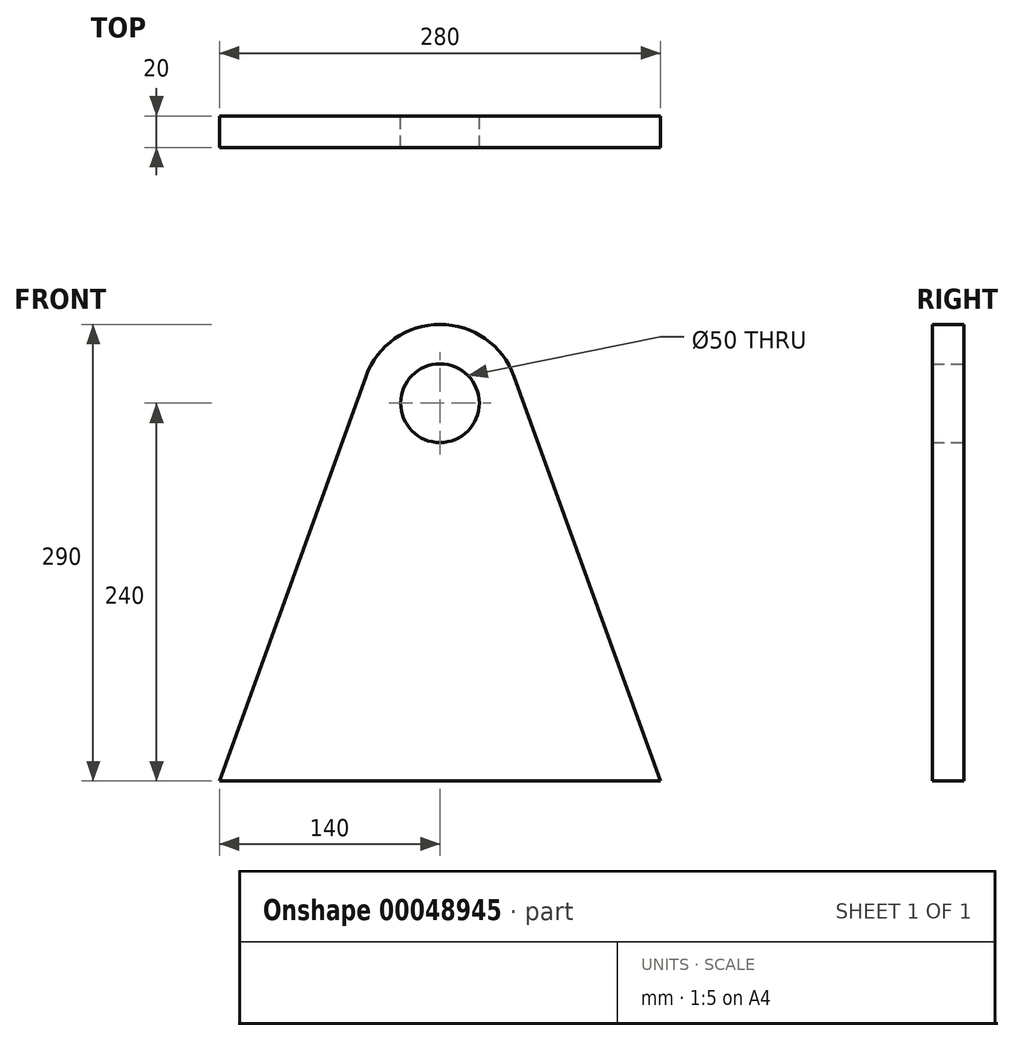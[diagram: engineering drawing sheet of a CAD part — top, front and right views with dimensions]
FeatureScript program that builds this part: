
annotation { "Feature Type Name" : "Feature", "Feature Type Description" : "" }
export const myFeature = defineFeature(function(context is Context, id is Id, definition is map)
    precondition{}
    {
        {
            var Q0;
            Q0=qCreatedBy(makeId("Front.planeOp"),FACE);
            var sketch = newSketch(context, id + "F0", { "sketchPlane" : qUnion([Q0])});
            skLineSegment(sketch, "E0", {"start": v(0, 240) * mm, "end": v(0, 0) * mm, "construction": true});
            skLineSegment(sketch, "E1", {"start": v(0, 0) * mm, "end": v(-140, 0) * mm});
            skLineSegment(sketch, "E2", {"start": v(-53.17, 240) * mm, "end": v(0, 240) * mm, "construction": true});
            skLineSegment(sketch, "E3", {"start": v(0, 240) * mm, "end": v(0, 290) * mm, "construction": true});
            skArc(sketch, "E4", {"start": v(0, 290) * mm, "mid": v(-28.72, 280.93) * mm, "end": v(-47.02, 257.01) * mm});
            skLineSegment(sketch, "E5", {"start": v(-140, 0) * mm, "end": v(-47.02, 257.01) * mm});
            skLineSegment(sketch, "E6.MirrorCS", {"start": v(0, 0) * mm, "end": v(140, 0) * mm});
            skLineSegment(sketch, "E7.MirrorCS", {"start": v(140, 0) * mm, "end": v(47.02, 257.01) * mm});
            skArc(sketch, "E8.MirrorCS", {"start": v(0, 290) * mm, "mid": v(28.72, 280.93) * mm, "end": v(47.02, 257.01) * mm});
            skCircle(sketch, "E9", {"center": v(0, 240) * mm, "radius": 25 * mm});
            skSolve(sketch);
        }
        {
            var Q0;
            Q0=makeQuery(id+"F0.imprint","IMPRINT",FACE,{"disambiguationData":[TD([[makeQuery(id+"F0.imprint","IMPRINT",EDGE,{"derivedFrom":sQuery(id+"F0.wireOp",EDGE,"E1")}),-1.0]])]});
            extrude(context, id + "F1", {"entities" : qUnion([Q0]), "depth" : 20 * mm});
        }
    });
